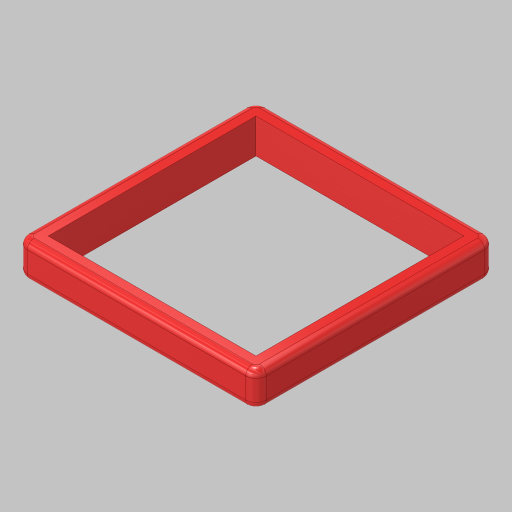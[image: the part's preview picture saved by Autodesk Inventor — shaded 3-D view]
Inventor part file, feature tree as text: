
AUTODESK INVENTOR PART (.ipt)
format: ipt  version: 2023.5 (Build 275446000, 446)  size: 155,648 bytes
history: native  units: in
note: dims shown in document units (in); Inventor stores cm internally (conversion verified against a paired STEP export)
features: fillet x2, extrude x1, sketch x1
ambient origin geometry x8: Origin, YZ Plane, XZ Plane, XY Plane, X Axis, Y Axis, Z Axis, Center Point
bodies: Solid1 (feature_tree)
feature tree (4):
  extrude  "Extrusion1"  Depth=30.0in
  fillet  "Fillet1"  Radius=2.25in
  fillet  "Fillet2"  Radius=5.0in
  sketch  "Sketch1"  dims[d0=30.0in d1=30.0in d2=2.25in d3=5.0in d4=0.0in d5=1.5in d6=1.0in]
